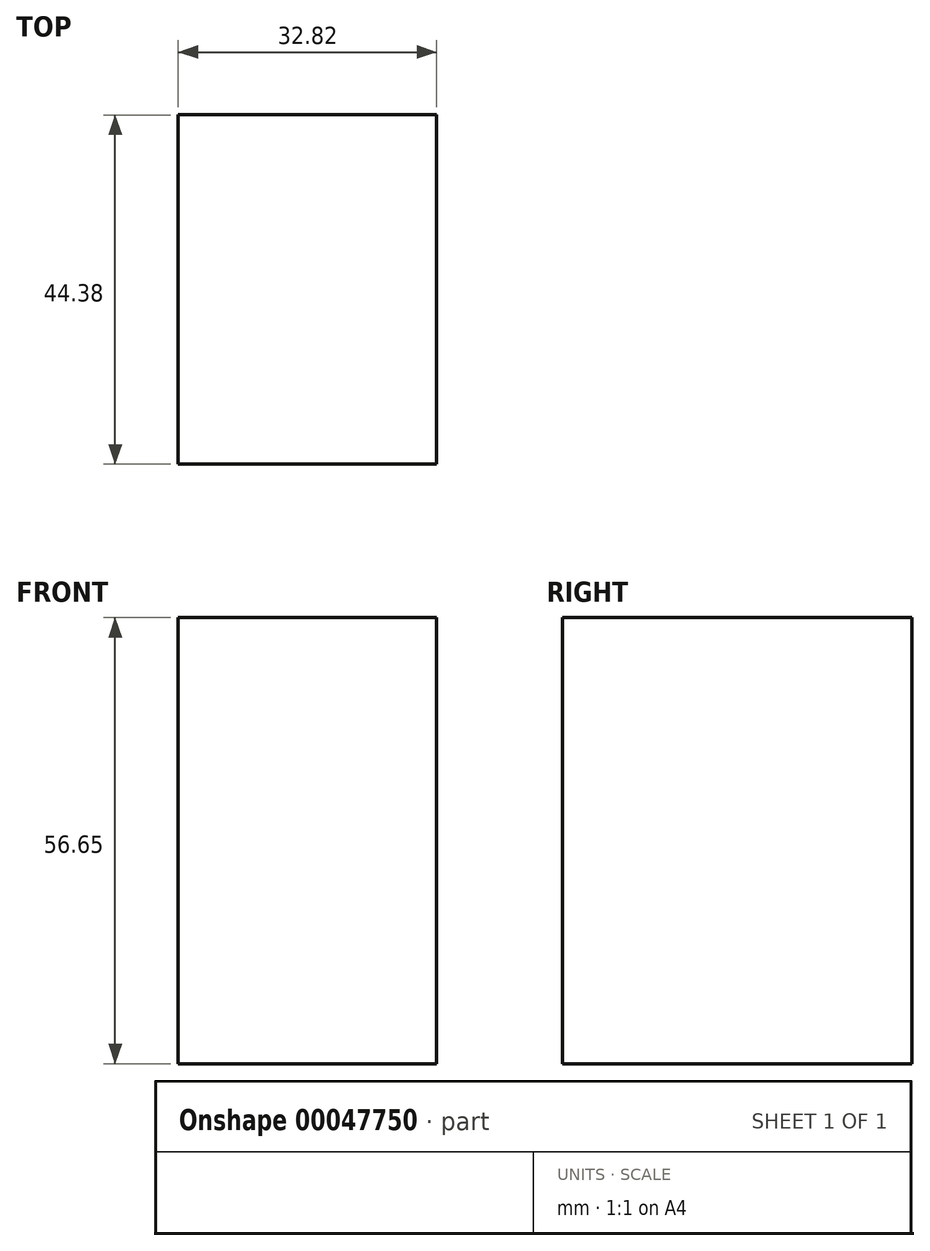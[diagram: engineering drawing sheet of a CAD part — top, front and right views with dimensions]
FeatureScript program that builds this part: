
annotation { "Feature Type Name" : "Feature", "Feature Type Description" : "" }
export const myFeature = defineFeature(function(context is Context, id is Id, definition is map)
    precondition{}
    {
        {
            var Q0;
            Q0=qCreatedBy(makeId("Top.planeOp"),FACE);
            var sketch = newSketch(context, id + "F0", { "sketchPlane" : qUnion([Q0])});
            skLineSegment(sketch, "E0.bottom", {"start": v(0, 0) * mm, "end": v(-32.82, 0) * mm});
            skLineSegment(sketch, "E0.top", {"start": v(0, 44.38) * mm, "end": v(-32.82, 44.38) * mm});
            skLineSegment(sketch, "E0.left", {"start": v(0, 0) * mm, "end": v(0, 44.38) * mm});
            skLineSegment(sketch, "E0.right", {"start": v(-32.82, 0) * mm, "end": v(-32.82, 44.38) * mm});
            skSolve(sketch);
        }
        {
            var Q0;
            Q0 = qSketchRegion(id + "F0", true);
            extrude(context, id + "F1", {"entities" : qUnion([Q0]), "depth" : 56.65 * mm});
        }
    });
